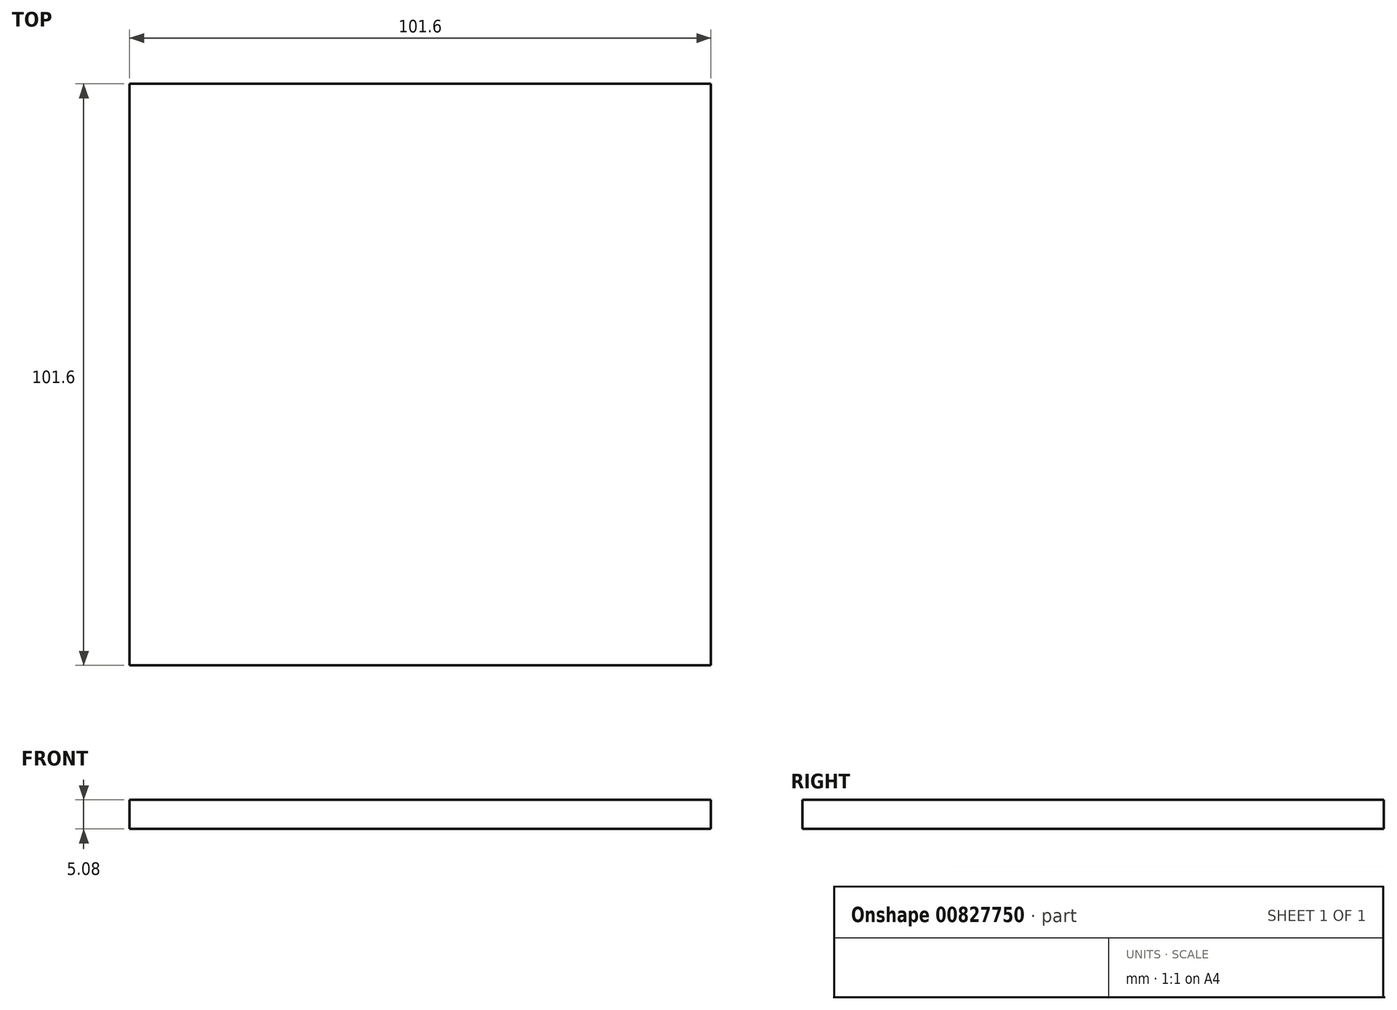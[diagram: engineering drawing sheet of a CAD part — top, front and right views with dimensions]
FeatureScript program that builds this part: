
annotation { "Feature Type Name" : "Feature", "Feature Type Description" : "" }
export const myFeature = defineFeature(function(context is Context, id is Id, definition is map)
    precondition{}
    {
        {
            var Q0;
            Q0=qCreatedBy(makeId("Top.planeOp"),FACE);
            var sketch = newSketch(context, id + "F0", { "sketchPlane" : qUnion([Q0])});
            skLineSegment(sketch, "E0", {"start": v(-41.36, 33.84) * mm, "end": v(60.24, 33.84) * mm});
            skLineSegment(sketch, "E1", {"start": v(60.24, 33.84) * mm, "end": v(60.24, -67.76) * mm});
            skLineSegment(sketch, "E2", {"start": v(60.24, -67.76) * mm, "end": v(-41.36, -67.76) * mm});
            skLineSegment(sketch, "E3", {"start": v(-41.36, -67.76) * mm, "end": v(-41.36, 33.84) * mm});
            skSolve(sketch);
        }
        {
            var Q0;
            Q0=makeQuery(id+"F0.imprint","IMPRINT",FACE,{"disambiguationData":[TD([[makeQuery(id+"F0.imprint","IMPRINT",EDGE,{"derivedFrom":sQuery(id+"F0.wireOp",EDGE,"E0")}),-1.0]])]});
            extrude(context, id + "F1", {"entities" : qUnion([Q0]), "depth" : 5.08 * mm, "offsetDistance" : 25.4 * mm});
        }
    });
